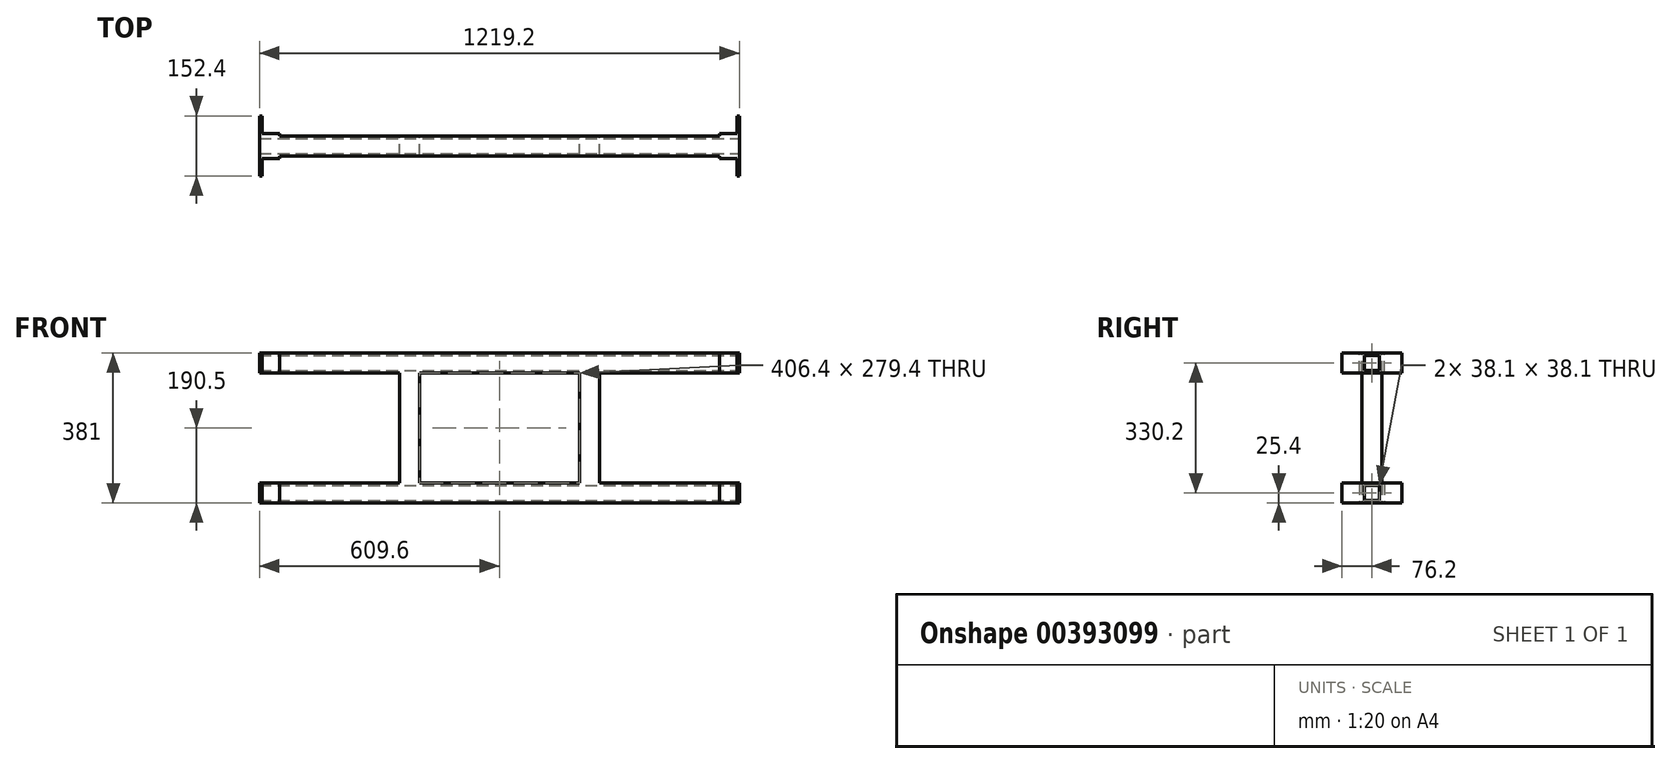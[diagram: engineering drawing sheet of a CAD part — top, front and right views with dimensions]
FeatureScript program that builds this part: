
annotation { "Feature Type Name" : "Feature", "Feature Type Description" : "" }
export const myFeature = defineFeature(function(context is Context, id is Id, definition is map)
    precondition{}
    {
        {
            var Q0;
            Q0=qCreatedBy(makeId("Front.planeOp"),FACE);
            var sketch = newSketch(context, id + "F0", { "sketchPlane" : qUnion([Q0])});
            skLineSegment(sketch, "E0.bottom", {"start": v(-609.6, 355.6) * mm, "end": v(609.6, 355.6) * mm, "construction": true});
            skLineSegment(sketch, "E0.top", {"start": v(-609.6, -355.6) * mm, "end": v(609.6, -355.6) * mm, "construction": true});
            skLineSegment(sketch, "E0.left", {"start": v(-609.6, 355.6) * mm, "end": v(-609.6, -355.6) * mm, "construction": true});
            skLineSegment(sketch, "E0.right", {"start": v(609.6, 355.6) * mm, "end": v(609.6, -355.6) * mm, "construction": true});
            skPoint(sketch, "E0.middle", {"position": v(0, 0) * mm});
            skLineSegment(sketch, "E1", {"start": v(-609.6, 0) * mm, "end": v(609.6, 0) * mm, "construction": true});
            skLineSegment(sketch, "E2.bottom", {"start": v(-609.6, 25.4) * mm, "end": v(-254, 25.4) * mm});
            skLineSegment(sketch, "E2.top", {"start": v(-609.6, -25.4) * mm, "end": v(609.6, -25.4) * mm});
            skLineSegment(sketch, "E2.left", {"start": v(-609.6, 25.4) * mm, "end": v(-609.6, -25.4) * mm});
            skLineSegment(sketch, "E2.right", {"start": v(609.6, 25.4) * mm, "end": v(609.6, -25.4) * mm});
            skLineSegment(sketch, "E3.bottom", {"start": v(-609.6, 355.6) * mm, "end": v(609.6, 355.6) * mm});
            skLineSegment(sketch, "E3.top", {"start": v(-609.6, 304.8) * mm, "end": v(-254, 304.8) * mm});
            skLineSegment(sketch, "E3.left", {"start": v(-609.6, 355.6) * mm, "end": v(-609.6, 304.8) * mm});
            skLineSegment(sketch, "E3.right", {"start": v(609.6, 355.6) * mm, "end": v(609.6, 304.8) * mm});
            skLineSegment(sketch, "E4", {"start": v(0, 0) * mm, "end": v(0, 355.6) * mm, "construction": true});
            skLineSegment(sketch, "E5.left", {"start": v(-254, 304.8) * mm, "end": v(-254, 25.4) * mm});
            skLineSegment(sketch, "E5.right", {"start": v(-203.2, 304.8) * mm, "end": v(-203.2, 25.4) * mm});
            skLineSegment(sketch, "E6.left", {"start": v(203.2, 304.8) * mm, "end": v(203.2, 25.4) * mm});
            skLineSegment(sketch, "E6.right", {"start": v(254, 304.8) * mm, "end": v(254, 25.4) * mm});
            skLineSegment(sketch, "E7", {"start": v(-203.2, 209.08) * mm, "end": v(0, 209.08) * mm, "construction": true});
            skLineSegment(sketch, "E8", {"start": v(0, 209.08) * mm, "end": v(203.2, 209.08) * mm, "construction": true});
            skLineSegment(sketch, "E9", {"start": v(-254, 209.72) * mm, "end": v(-609.6, 209.72) * mm, "construction": true});
            skLineSegment(sketch, "E10.trimOffspring", {"start": v(-203.2, 304.8) * mm, "end": v(203.2, 304.8) * mm});
            skLineSegment(sketch, "E11.trimOffspring", {"start": v(-203.2, 25.4) * mm, "end": v(203.2, 25.4) * mm});
            skLineSegment(sketch, "E12.trimOffspring", {"start": v(254, 304.8) * mm, "end": v(609.6, 304.8) * mm});
            skLineSegment(sketch, "E13.trimOffspring", {"start": v(254, 25.4) * mm, "end": v(609.6, 25.4) * mm});
            skSolve(sketch);
        }
        {
            var Q0;
            Q0 = qSketchRegion(id + "F0", true);
            extrude(context, id + "F1", {"entities" : qUnion([Q0]), "endBound" : BoundingType.SYMMETRIC, "depth" : 50.8 * mm});
        }
        {
            var Q0;
            Q0=makeQuery(id+"F1.opExtrude","SWEPT_FACE",FACE,{"disambiguationData":[OSD([sQuery(id+"F0.wireOp",EDGE,"E3.bottom")])]});
            var sketch = newSketch(context, id + "F2", { "sketchPlane" : qUnion([Q0])});
            skLineSegment(sketch, "E14.bottom", {"start": v(-609.6, 25.4) * mm, "end": v(-603.25, 25.4) * mm});
            skLineSegment(sketch, "E14.top", {"start": v(-609.6, 76.2) * mm, "end": v(-603.25, 76.2) * mm});
            skLineSegment(sketch, "E14.left", {"start": v(-609.6, 25.4) * mm, "end": v(-609.6, 76.2) * mm});
            skLineSegment(sketch, "E14.right", {"start": v(-603.25, 31.75) * mm, "end": v(-603.25, 76.2) * mm});
            skLineSegment(sketch, "E15.bottom", {"start": v(-603.25, 25.4) * mm, "end": v(-558.8, 25.4) * mm});
            skLineSegment(sketch, "E15.top", {"start": v(-603.25, 31.75) * mm, "end": v(-558.8, 31.75) * mm});
            skLineSegment(sketch, "E15.right", {"start": v(-558.8, 25.4) * mm, "end": v(-558.8, 31.75) * mm});
            skLineSegment(sketch, "E16.MirrorCS", {"start": v(-609.6, -76.2) * mm, "end": v(-603.25, -76.2) * mm});
            skLineSegment(sketch, "E17.MirrorCS", {"start": v(-609.6, -25.4) * mm, "end": v(-603.25, -25.4) * mm});
            skLineSegment(sketch, "E18.MirrorCS", {"start": v(-558.8, -25.4) * mm, "end": v(-558.8, -31.75) * mm});
            skLineSegment(sketch, "E19.MirrorCS", {"start": v(-603.25, -31.75) * mm, "end": v(-558.8, -31.75) * mm});
            skLineSegment(sketch, "E20.MirrorCS", {"start": v(-603.25, -25.4) * mm, "end": v(-558.8, -25.4) * mm});
            skLineSegment(sketch, "E21.MirrorCS", {"start": v(-609.6, -25.4) * mm, "end": v(-609.6, -76.2) * mm});
            skLineSegment(sketch, "E22.MirrorCS", {"start": v(-603.25, -31.75) * mm, "end": v(-603.25, -76.2) * mm});
            skLineSegment(sketch, "E23.MirrorCS", {"start": v(558.8, -25.4) * mm, "end": v(558.8, -31.75) * mm});
            skLineSegment(sketch, "E24.MirrorCS", {"start": v(609.6, 25.4) * mm, "end": v(603.25, 25.4) * mm});
            skLineSegment(sketch, "E25.MirrorCS", {"start": v(609.6, 76.2) * mm, "end": v(603.25, 76.2) * mm});
            skLineSegment(sketch, "E26.MirrorCS", {"start": v(609.6, -76.2) * mm, "end": v(603.25, -76.2) * mm});
            skLineSegment(sketch, "E27.MirrorCS", {"start": v(609.6, -25.4) * mm, "end": v(603.25, -25.4) * mm});
            skLineSegment(sketch, "E28.MirrorCS", {"start": v(558.8, 25.4) * mm, "end": v(558.8, 31.75) * mm});
            skLineSegment(sketch, "E29.MirrorCS", {"start": v(609.6, -25.4) * mm, "end": v(609.6, -76.2) * mm});
            skLineSegment(sketch, "E30.MirrorCS", {"start": v(603.25, -31.75) * mm, "end": v(603.25, -76.2) * mm});
            skLineSegment(sketch, "E31.MirrorCS", {"start": v(603.25, 31.75) * mm, "end": v(603.25, 76.2) * mm});
            skLineSegment(sketch, "E32.MirrorCS", {"start": v(603.25, -31.75) * mm, "end": v(558.8, -31.75) * mm});
            skLineSegment(sketch, "E33.MirrorCS", {"start": v(603.25, -25.4) * mm, "end": v(558.8, -25.4) * mm});
            skLineSegment(sketch, "E34.MirrorCS", {"start": v(603.25, 25.4) * mm, "end": v(558.8, 25.4) * mm});
            skLineSegment(sketch, "E35.MirrorCS", {"start": v(609.6, 25.4) * mm, "end": v(609.6, 76.2) * mm});
            skLineSegment(sketch, "E36.MirrorCS", {"start": v(603.25, 31.75) * mm, "end": v(558.8, 31.75) * mm});
            skSolve(sketch);
        }
        {
            var Q0;
            Q0 = qSketchRegion(id + "F2", true);
            extrude(context, id + "F3", {"entities" : qUnion([Q0]), "operationType" : NewBodyOperationType.ADD, "oppositeDirection" : true, "depth" : 50.8 * mm});
        }
        {
            var Q0;
            Q0=makeQuery(id+"F1.opExtrude","SWEPT_FACE",FACE,{"disambiguationData":[OSD([sQuery(id+"F0.wireOp",EDGE,"E2.top")])]});
            var sketch = newSketch(context, id + "F4", { "sketchPlane" : qUnion([Q0])});
            skLineSegment(sketch, "E37.0", {"start": v(-603.25, -31.75) * mm, "end": v(-603.25, -76.2) * mm});
            skLineSegment(sketch, "E37.1", {"start": v(-603.25, -31.75) * mm, "end": v(-558.8, -31.75) * mm});
            skLineSegment(sketch, "E37.2", {"start": v(-603.25, 31.75) * mm, "end": v(-558.8, 31.75) * mm});
            skLineSegment(sketch, "E37.3", {"start": v(-603.25, 25.4) * mm, "end": v(-558.8, 25.4) * mm});
            skLineSegment(sketch, "E37.4", {"start": v(-603.25, -25.4) * mm, "end": v(-558.8, -25.4) * mm});
            skLineSegment(sketch, "E37.5", {"start": v(-609.6, 25.4) * mm, "end": v(-609.6, 76.2) * mm});
            skLineSegment(sketch, "E37.6", {"start": v(-603.25, 31.75) * mm, "end": v(-603.25, 76.2) * mm});
            skLineSegment(sketch, "E37.7", {"start": v(-609.6, -25.4) * mm, "end": v(-609.6, -76.2) * mm});
            skLineSegment(sketch, "E37.8", {"start": v(-603.25, 31.75) * mm, "end": v(-603.25, 76.2) * mm});
            skLineSegment(sketch, "E37.9", {"start": v(-603.25, 31.75) * mm, "end": v(-558.8, 31.75) * mm});
            skLineSegment(sketch, "E37.10", {"start": v(-609.6, 25.4) * mm, "end": v(-609.6, 76.2) * mm});
            skLineSegment(sketch, "E37.11", {"start": v(-603.25, -31.75) * mm, "end": v(-603.25, -76.2) * mm});
            skLineSegment(sketch, "E37.12", {"start": v(-603.25, -31.75) * mm, "end": v(-558.8, -31.75) * mm});
            skLineSegment(sketch, "E37.13", {"start": v(-603.25, -25.4) * mm, "end": v(-558.8, -25.4) * mm});
            skLineSegment(sketch, "E38.0", {"start": v(603.25, 25.4) * mm, "end": v(558.8, 25.4) * mm});
            skLineSegment(sketch, "E38.1", {"start": v(603.25, -31.75) * mm, "end": v(603.25, -76.2) * mm});
            skLineSegment(sketch, "E38.2", {"start": v(609.6, -25.4) * mm, "end": v(609.6, -76.2) * mm});
            skLineSegment(sketch, "E38.3", {"start": v(609.6, 25.4) * mm, "end": v(609.6, 76.2) * mm});
            skLineSegment(sketch, "E38.4", {"start": v(603.25, 31.75) * mm, "end": v(558.8, 31.75) * mm});
            skLineSegment(sketch, "E38.5", {"start": v(603.25, -31.75) * mm, "end": v(558.8, -31.75) * mm});
            skLineSegment(sketch, "E38.6", {"start": v(603.25, 31.75) * mm, "end": v(603.25, 76.2) * mm});
            skLineSegment(sketch, "E38.7", {"start": v(603.25, -25.4) * mm, "end": v(558.8, -25.4) * mm});
            skLineSegment(sketch, "E38.8", {"start": v(603.25, 25.4) * mm, "end": v(558.8, 25.4) * mm});
            skLineSegment(sketch, "E38.9", {"start": v(609.6, -25.4) * mm, "end": v(609.6, -76.2) * mm});
            skLineSegment(sketch, "E38.10", {"start": v(603.25, -31.75) * mm, "end": v(603.25, -76.2) * mm});
            skLineSegment(sketch, "E38.11", {"start": v(609.6, 25.4) * mm, "end": v(609.6, 76.2) * mm});
            skLineSegment(sketch, "E38.12", {"start": v(603.25, 31.75) * mm, "end": v(558.8, 31.75) * mm});
            skLineSegment(sketch, "E38.13", {"start": v(603.25, 31.75) * mm, "end": v(603.25, 76.2) * mm});
            skLineSegment(sketch, "E39", {"start": v(-609.6, 76.2) * mm, "end": v(-603.25, 76.2) * mm});
            skLineSegment(sketch, "E40", {"start": v(-558.8, 31.75) * mm, "end": v(-558.8, 25.4) * mm});
            skLineSegment(sketch, "E41", {"start": v(-558.8, -25.4) * mm, "end": v(-558.8, -31.75) * mm});
            skLineSegment(sketch, "E42", {"start": v(-609.6, -76.2) * mm, "end": v(-603.25, -76.2) * mm});
            skLineSegment(sketch, "E43", {"start": v(603.25, 76.2) * mm, "end": v(609.6, 76.2) * mm});
            skLineSegment(sketch, "E44", {"start": v(558.8, 31.75) * mm, "end": v(558.8, 25.4) * mm});
            skLineSegment(sketch, "E45", {"start": v(558.8, -25.4) * mm, "end": v(558.8, -31.75) * mm});
            skLineSegment(sketch, "E46", {"start": v(603.25, -76.2) * mm, "end": v(609.6, -76.2) * mm});
            skLineSegment(sketch, "E47", {"start": v(-609.6, 25.4) * mm, "end": v(-603.25, 25.4) * mm});
            skLineSegment(sketch, "E48", {"start": v(-609.6, -25.4) * mm, "end": v(-603.25, -25.4) * mm});
            skLineSegment(sketch, "E49", {"start": v(603.25, 25.4) * mm, "end": v(609.6, 25.4) * mm});
            skLineSegment(sketch, "E50", {"start": v(603.25, -25.4) * mm, "end": v(609.6, -25.4) * mm});
            skSolve(sketch);
        }
        {
            var Q0;
            Q0 = qSketchRegion(id + "F4", true);
            extrude(context, id + "F5", {"entities" : qUnion([Q0]), "operationType" : NewBodyOperationType.ADD, "oppositeDirection" : true, "depth" : 50.8 * mm});
        }
        {
            var Q0;
            Q0=qCreatedBy(makeId("Right.planeOp"),FACE);
            var sketch = newSketch(context, id + "F6", { "sketchPlane" : qUnion([Q0])});
            skLineSegment(sketch, "E51", {"start": v(76.2, 330.2) * mm, "end": v(-76.2, 330.2) * mm, "construction": true});
            skLineSegment(sketch, "E52", {"start": v(0, 355.6) * mm, "end": v(0, 304.8) * mm, "construction": true});
            skLineSegment(sketch, "E53.bottom", {"start": v(19.05, 349.25) * mm, "end": v(-19.05, 349.25) * mm});
            skLineSegment(sketch, "E53.top", {"start": v(19.05, 311.15) * mm, "end": v(-19.05, 311.15) * mm});
            skLineSegment(sketch, "E53.left", {"start": v(19.05, 349.25) * mm, "end": v(19.05, 311.15) * mm});
            skLineSegment(sketch, "E53.right", {"start": v(-19.05, 349.25) * mm, "end": v(-19.05, 311.15) * mm});
            skPoint(sketch, "E53.middle", {"position": v(0, 330.2) * mm});
            skLineSegment(sketch, "E54", {"start": v(25.4, 165.1) * mm, "end": v(-25.4, 165.1) * mm, "construction": true});
            skLineSegment(sketch, "E55.MirrorCS", {"start": v(19.05, -19.05) * mm, "end": v(-19.05, -19.05) * mm});
            skLineSegment(sketch, "E56.MirrorCS", {"start": v(19.05, -19.05) * mm, "end": v(19.05, 19.05) * mm});
            skLineSegment(sketch, "E57.MirrorCS", {"start": v(19.05, 19.05) * mm, "end": v(-19.05, 19.05) * mm});
            skLineSegment(sketch, "E58.MirrorCS", {"start": v(-19.05, -19.05) * mm, "end": v(-19.05, 19.05) * mm});
            skPoint(sketch, "E59.MirrorP", {"position": v(0, 0) * mm});
            skPoint(sketch, "E60.orphan", {"position": v(-76.2, 355.6) * mm});
            skPoint(sketch, "E61.0.0.end.orphan", {"position": v(76.2, 355.6) * mm});
            skPoint(sketch, "E62.orphan", {"position": v(76.2, 304.8) * mm});
            skPoint(sketch, "E63.orphan", {"position": v(-76.2, 304.8) * mm});
            skPoint(sketch, "E64.0.3.start.orphan", {"position": v(-25.4, 304.8) * mm});
            skPoint(sketch, "E61.0.2.start.orphan", {"position": v(25.4, 304.8) * mm});
            skPoint(sketch, "E65.orphan", {"position": v(76.2, 25.4) * mm});
            skPoint(sketch, "E64.0.1.end.orphan", {"position": v(-25.4, 25.4) * mm});
            skPoint(sketch, "E66.orphan", {"position": v(-76.2, 25.4) * mm});
            skPoint(sketch, "E67.0.end.orphan", {"position": v(25.4, 25.4) * mm});
            skPoint(sketch, "E68.0.end.orphan", {"position": v(76.2, -25.4) * mm});
            skPoint(sketch, "E68.0.start.orphan", {"position": v(-76.2, -25.4) * mm});
            skSolve(sketch);
        }
        {
            var Q0;
            Q0 = qSketchRegion(id + "F6", true);
            extrude(context, id + "F7", {"entities" : qUnion([Q0]), "operationType" : NewBodyOperationType.REMOVE, "endBound" : BoundingType.SYMMETRIC, "oppositeDirection" : true, "depth" : 2540 * mm});
        }
    });
